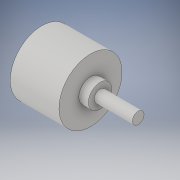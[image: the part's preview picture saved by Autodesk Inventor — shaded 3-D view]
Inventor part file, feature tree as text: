
AUTODESK INVENTOR PART (.ipt)
format: ipt  version: 2019 (Build 230136000, 136)  size: 117,760 bytes
history: native  units: in
note: dims shown in document units (in); Inventor stores cm internally (conversion verified against a paired STEP export)
features: sketch x3, extrude x2, sheet_metal_op x1, other x1
ambient origin geometry x8: Origin, YZ Plane, XZ Plane, XY Plane, X Axis, Y Axis, Z Axis, Center Point
bodies: Solid1 (feature_tree)
feature tree (7):
  sheet_metal_op  "Face1"
  extrude  "Extrusion1"  Depth=1.0039in
  extrude  "Extrusion2"  Depth=0.1969in TaperAngle=0.0deg
  sketch  "Sketch1"  dims[d0=1.2992in d1=1.0039in]
  other  "Plate1"
  sketch  "Sketch2"  dims[d2=0.4803in d3=0.1969in d4=0.0in]
  sketch  "Sketch3"  dims[d5=0.2401in d6=0.7874in d7=0.0in]
